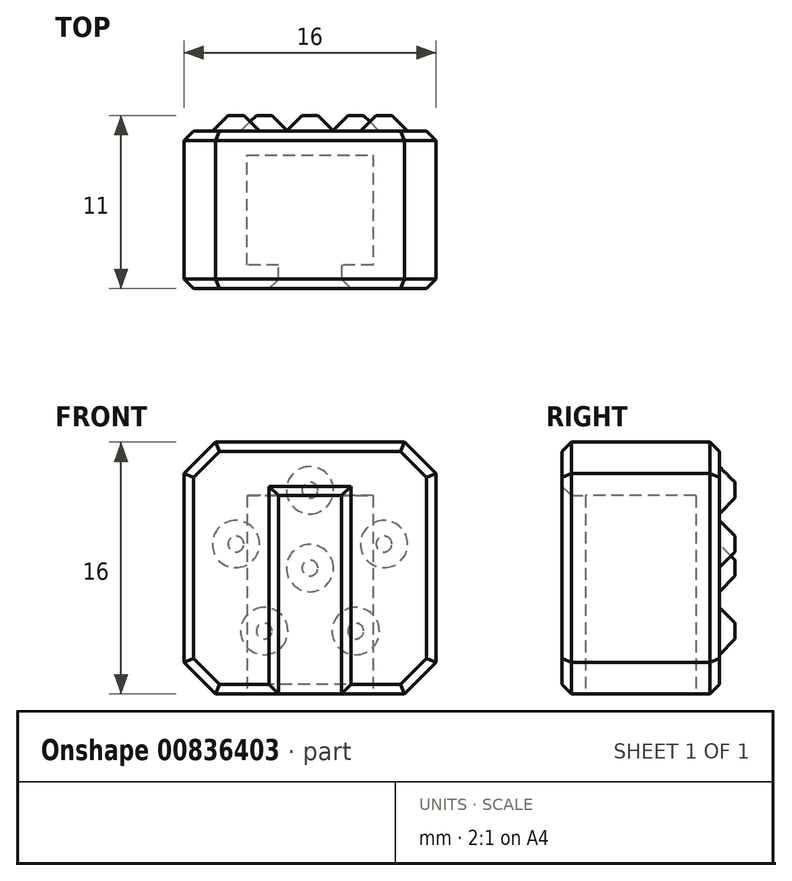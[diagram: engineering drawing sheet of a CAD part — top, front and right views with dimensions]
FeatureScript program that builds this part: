
annotation { "Feature Type Name" : "Feature", "Feature Type Description" : "" }
export const myFeature = defineFeature(function(context is Context, id is Id, definition is map)
    precondition{}
    {
        {
            assignVariable(context, id + "F0", {"name" : "Head", "anyValue" : 16});
        }
        {
            var Q0;
            Q0=qCreatedBy(makeId("Top.planeOp"),FACE);
            var sketch = newSketch(context, id + "F1", { "sketchPlane" : qUnion([Q0])});
            skLineSegment(sketch, "E0", {"start": v(-2, -5) * mm, "end": v(-2, -3.5) * mm});
            skLineSegment(sketch, "E1", {"start": v(-2, -3.5) * mm, "end": v(-4, -3.5) * mm});
            skLineSegment(sketch, "E2", {"start": v(-4, -3.5) * mm, "end": v(-4, 3.5) * mm});
            skLineSegment(sketch, "E3", {"start": v(-4, 3.5) * mm, "end": v(4, 3.5) * mm});
            skLineSegment(sketch, "E4", {"start": v(4, 3.5) * mm, "end": v(4, -3.5) * mm});
            skLineSegment(sketch, "E5", {"start": v(4, -3.5) * mm, "end": v(2, -3.5) * mm});
            skLineSegment(sketch, "E6", {"start": v(2, -3.5) * mm, "end": v(2, -5) * mm});
            skLineSegment(sketch, "E7", {"start": v(2, -5) * mm, "end": v(8, -5) * mm});
            skLineSegment(sketch, "E8", {"start": v(8, -5) * mm, "end": v(8, 5) * mm});
            skLineSegment(sketch, "E9", {"start": v(8, 5) * mm, "end": v(-8, 5) * mm});
            skLineSegment(sketch, "E10", {"start": v(-8, 5) * mm, "end": v(-8, -5) * mm});
            skLineSegment(sketch, "E11", {"start": v(-8, -5) * mm, "end": v(-2, -5) * mm});
            skLineSegment(sketch, "E12", {"start": v(-4, -3.5) * mm, "end": v(0, 0) * mm, "construction": true});
            skLineSegment(sketch, "E13", {"start": v(0, 0) * mm, "end": v(4, 3.5) * mm, "construction": true});
            skLineSegment(sketch, "E14", {"start": v(4, -3.5) * mm, "end": v(0, 0) * mm, "construction": true});
            skLineSegment(sketch, "E15", {"start": v(-4, 3.5) * mm, "end": v(0, 0) * mm, "construction": true});
            skLineSegment(sketch, "E16", {"start": v(-2, -3.5) * mm, "end": v(0, 0) * mm, "construction": true});
            skLineSegment(sketch, "E17", {"start": v(2, -3.5) * mm, "end": v(0, 0) * mm, "construction": true});
            skLineSegment(sketch, "E18", {"start": v(4, 3.5) * mm, "end": v(8, 3.5) * mm, "construction": true});
            skLineSegment(sketch, "E19", {"start": v(-4, 3.5) * mm, "end": v(-8, 3.5) * mm, "construction": true});
            skLineSegment(sketch, "E20", {"start": v(-2, -5) * mm, "end": v(2, -5) * mm});
            skSolve(sketch);
        }
        {
            var Q0;
            Q0=makeQuery(id+"F1.imprint","IMPRINT",FACE,{"disambiguationData":[TD([[makeQuery(id+"F1.imprint","IMPRINT",EDGE,{"derivedFrom":sQuery(id+"F1.wireOp",EDGE,"E0")}),1.0]])]});
            var Q1;
            Q1=makeQuery(id+"F1.imprint","IMPRINT",FACE,{"disambiguationData":[TD([[makeQuery(id+"F1.imprint","IMPRINT",EDGE,{"derivedFrom":sQuery(id+"F1.wireOp",EDGE,"E0")}),-1.0]])]});
            extrude(context, id + "F2", {"entities" : qUnion([Q0, Q1]), "depth" : (getVariable(context, 'Head')) * mm, "offsetDistance" : 25 * mm});
        }
        {
            var Q0;
            Q0=makeQuery(id+"F1.imprint","IMPRINT",FACE,{"disambiguationData":[TD([[makeQuery(id+"F1.imprint","IMPRINT",EDGE,{"derivedFrom":sQuery(id+"F1.wireOp",EDGE,"E0")}),-1.0]])]});
            extrude(context, id + "F3", {"entities" : qUnion([Q0]), "operationType" : NewBodyOperationType.REMOVE, "depth" : (getVariable(context, 'Head') / 2 + 4.6) * mm, "offsetDistance" : 25 * mm});
        }
        {
            var Q0;
            Q0=makeQuery(id+"F2.opExtrude","CAP_EDGE",EDGE,{"disambiguationData":[OSD([sQuery(id+"F1.wireOp",EDGE,"E10")])],"isStart":true});
            var Q1;
            Q1=makeQuery(id+"F2.opExtrude","CAP_EDGE",EDGE,{"disambiguationData":[OSD([sQuery(id+"F1.wireOp",EDGE,"E10")])],"isStart":false});
            var Q2;
            Q2=makeQuery(id+"F2.opExtrude","CAP_EDGE",EDGE,{"disambiguationData":[OSD([sQuery(id+"F1.wireOp",EDGE,"E8")])],"isStart":false});
            var Q3;
            Q3=makeQuery(id+"F2.opExtrude","CAP_EDGE",EDGE,{"disambiguationData":[OSD([sQuery(id+"F1.wireOp",EDGE,"E8")])],"isStart":true});
            chamfer(context, id + "F4", {"entities" : qUnion([Q0, Q1, Q2, Q3]), "width" : 2 * mm, "tangentPropagation" : true});
        }
        {
            var Q0;
            Q0=makeQuery(id+"F2.opExtrude","SWEPT_FACE",FACE,{"disambiguationData":[OSD([sQuery(id+"F1.wireOp",EDGE,"E9")])]});
            var Q1;
            Q1=makeQuery(id+"F2.opExtrude","SWEPT_FACE",FACE,{"disambiguationData":[OSD([sQuery(id+"F1.wireOp",EDGE,"E7"),sQuery(id+"F1.wireOp",EDGE,"E11"),sQuery(id+"F1.wireOp",EDGE,"E20")])]});
            chamfer(context, id + "F5", {"entities" : qUnion([Q0, Q1]), "width" : 0.6 * mm, "tangentPropagation" : true});
        }
        {
            var Q0;
            Q0=makeQuery(id+"F2.opExtrude","SWEPT_FACE",FACE,{"disambiguationData":[OSD([sQuery(id+"F1.wireOp",EDGE,"E9")])]});
            var sketch = newSketch(context, id + "F6", { "sketchPlane" : qUnion([Q0])});
            skPoint(sketch, "E21.0", {"position": v(0, 0) * mm});
            skLineSegment(sketch, "E22", {"start": v(0, 0) * mm, "end": v(0, 8) * mm, "construction": true});
            skCircle(sketch, "E23.cCircle", {"center": v(0, 8) * mm, "radius": 4 * mm, "construction": true});
            skLineSegment(sketch, "E23.0", {"start": v(2.9, 4) * mm, "end": v(-2.9, 4) * mm, "construction": true});
            skLineSegment(sketch, "E23.1", {"start": v(-2.9, 4) * mm, "end": v(-4.7, 9.53) * mm, "construction": true});
            skLineSegment(sketch, "E23.2", {"start": v(-4.7, 9.53) * mm, "end": v(0, 12.94) * mm, "construction": true});
            skLineSegment(sketch, "E23.3", {"start": v(0, 12.94) * mm, "end": v(4.7, 9.53) * mm, "construction": true});
            skLineSegment(sketch, "E23.4", {"start": v(4.7, 9.53) * mm, "end": v(2.9, 4) * mm, "construction": true});
            skPoint(sketch, "E23.0.midPoint", {"position": v(0, 4) * mm});
            skCircle(sketch, "E24", {"center": v(0, 8) * mm, "radius": 1.5 * mm});
            skCircle(sketch, "E25", {"center": v(2.9, 4) * mm, "radius": 1.5 * mm});
            skCircle(sketch, "E26", {"center": v(4.7, 9.53) * mm, "radius": 1.5 * mm});
            skCircle(sketch, "E27", {"center": v(0, 12.94) * mm, "radius": 1.5 * mm});
            skCircle(sketch, "E28", {"center": v(-4.7, 9.53) * mm, "radius": 1.5 * mm});
            skCircle(sketch, "E29", {"center": v(-2.9, 4) * mm, "radius": 1.5 * mm});
            skSolve(sketch);
        }
        {
            var Q0;
            Q0=makeQuery(id+"F6.imprint","IMPRINT",FACE,{"disambiguationData":[TD([[makeQuery(id+"F6.imprint","IMPRINT",EDGE,{"derivedFrom":sQuery(id+"F6.wireOp",EDGE,"E29")}),1.0]])]});
            var Q1;
            Q1=makeQuery(id+"F6.imprint","IMPRINT",FACE,{"disambiguationData":[TD([[makeQuery(id+"F6.imprint","IMPRINT",EDGE,{"derivedFrom":sQuery(id+"F6.wireOp",EDGE,"E25")}),1.0]])]});
            var Q2;
            Q2=makeQuery(id+"F6.imprint","IMPRINT",FACE,{"disambiguationData":[TD([[makeQuery(id+"F6.imprint","IMPRINT",EDGE,{"derivedFrom":sQuery(id+"F6.wireOp",EDGE,"E26")}),1.0]])]});
            var Q3;
            Q3=makeQuery(id+"F6.imprint","IMPRINT",FACE,{"disambiguationData":[TD([[makeQuery(id+"F6.imprint","IMPRINT",EDGE,{"derivedFrom":sQuery(id+"F6.wireOp",EDGE,"E27")}),1.0]])]});
            var Q4;
            Q4=makeQuery(id+"F6.imprint","IMPRINT",FACE,{"disambiguationData":[TD([[makeQuery(id+"F6.imprint","IMPRINT",EDGE,{"derivedFrom":sQuery(id+"F6.wireOp",EDGE,"E28")}),1.0]])]});
            var Q5;
            Q5=makeQuery(id+"F6.imprint","IMPRINT",FACE,{"disambiguationData":[TD([[makeQuery(id+"F6.imprint","IMPRINT",EDGE,{"derivedFrom":sQuery(id+"F6.wireOp",EDGE,"E24")}),1.0]])]});
            extrude(context, id + "F7", {"entities" : qUnion([Q0, Q1, Q2, Q3, Q4, Q5]), "operationType" : NewBodyOperationType.ADD, "depth" : 1 * mm, "offsetDistance" : 25 * mm, "hasDraft" : true, "draftAngle" : 45 * degree, "draftPullDirection" : true});
        }
    });
